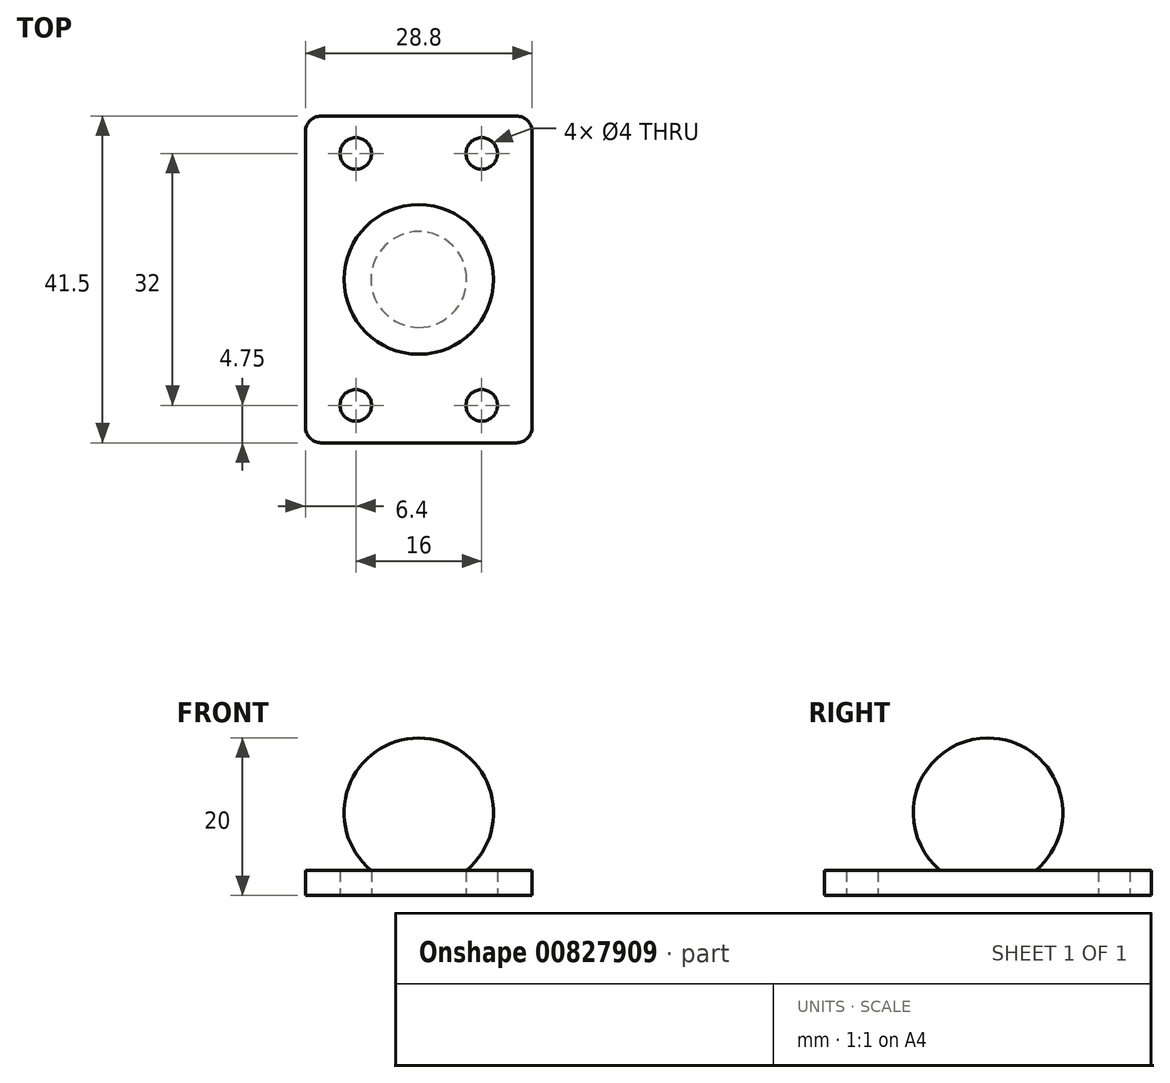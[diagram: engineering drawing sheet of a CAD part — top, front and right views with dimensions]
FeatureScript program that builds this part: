
annotation { "Feature Type Name" : "Feature", "Feature Type Description" : "" }
export const myFeature = defineFeature(function(context is Context, id is Id, definition is map)
    precondition{}
    {
        {
            var Q0;
            Q0=qCreatedBy(makeId("Top.planeOp"),FACE);
            var sketch = newSketch(context, id + "F0", { "sketchPlane" : qUnion([Q0])});
            skLineSegment(sketch, "E0.bottom", {"start": v(12.4, 20.75) * mm, "end": v(-12.4, 20.75) * mm});
            skLineSegment(sketch, "E0.top", {"start": v(12.4, -20.75) * mm, "end": v(-12.4, -20.75) * mm});
            skLineSegment(sketch, "E0.left", {"start": v(14.4, 18.75) * mm, "end": v(14.4, -18.75) * mm});
            skLineSegment(sketch, "E0.right", {"start": v(-14.4, 18.75) * mm, "end": v(-14.4, -18.75) * mm});
            skPoint(sketch, "E0.middle", {"position": v(0, 0) * mm});
            skLineSegment(sketch, "E1.bottom", {"start": v(8, 16) * mm, "end": v(-8, 16) * mm, "construction": true});
            skLineSegment(sketch, "E1.top", {"start": v(8, -16) * mm, "end": v(-8, -16) * mm, "construction": true});
            skLineSegment(sketch, "E1.left", {"start": v(8, 16) * mm, "end": v(8, -16) * mm, "construction": true});
            skLineSegment(sketch, "E1.right", {"start": v(-8, 16) * mm, "end": v(-8, -16) * mm, "construction": true});
            skCircle(sketch, "E2", {"center": v(-8, 16) * mm, "radius": 2 * mm});
            skCircle(sketch, "E3", {"center": v(8, 16) * mm, "radius": 2 * mm});
            skCircle(sketch, "E4", {"center": v(8, -16) * mm, "radius": 2 * mm});
            skCircle(sketch, "E5", {"center": v(-8, -16) * mm, "radius": 2 * mm});
            skPoint(sketch, "E6.visualSharp", {"position": v(-14.4, 20.75) * mm});
            skArc(sketch, "E6.filletArc", {"start": v(-12.4, 20.75) * mm, "mid": v(-13.81, 20.16) * mm, "end": v(-14.4, 18.75) * mm});
            skPoint(sketch, "E7.visualSharp", {"position": v(14.4, 20.75) * mm});
            skArc(sketch, "E7.filletArc", {"start": v(14.4, 18.75) * mm, "mid": v(13.81, 20.16) * mm, "end": v(12.4, 20.75) * mm});
            skPoint(sketch, "E8.visualSharp", {"position": v(14.4, -20.75) * mm});
            skArc(sketch, "E8.filletArc", {"start": v(12.4, -20.75) * mm, "mid": v(13.81, -20.16) * mm, "end": v(14.4, -18.75) * mm});
            skPoint(sketch, "E9.visualSharp", {"position": v(-14.4, -20.75) * mm});
            skArc(sketch, "E9.filletArc", {"start": v(-14.4, -18.75) * mm, "mid": v(-13.81, -20.16) * mm, "end": v(-12.4, -20.75) * mm});
            skSolve(sketch);
        }
        {
            var Q0;
            Q0 = qSketchRegion(id + "F0", true);
            extrude(context, id + "F1", {"entities" : qUnion([Q0]), "depth" : 3.2 * mm, "offsetDistance" : 25 * mm});
        }
        {
            var Q0;
            Q0=qCreatedBy(makeId("Right.planeOp"),FACE);
            var sketch = newSketch(context, id + "F2", { "sketchPlane" : qUnion([Q0])});
            skArc(sketch, "E10", {"start": v(0, 20) * mm, "mid": v(-9.5, 10.5) * mm, "end": v(0, 1) * mm});
            skPoint(sketch, "E11", {"position": v(0, 20) * mm});
            skLineSegment(sketch, "E12", {"start": v(0, 26.46) * mm, "end": v(0, 41.79) * mm, "construction": true});
            skLineSegment(sketch, "E13", {"start": v(0, 20) * mm, "end": v(0, 1) * mm});
            skSolve(sketch);
        }
        {
            var Q0;
            Q0 = qSketchRegion(id + "F2", true);
            var Q1;
            Q1=sQuery(id+"F2.wireOp",EDGE,"E12");
            revolve(context, id + "F3", {"operationType" : NewBodyOperationType.ADD, "surfaceOperationType" : NewSurfaceOperationType.NEW, "entities" : qUnion([Q0]), "axis" : qUnion([Q1]), "revolveType" : RevolveType.FULL});
        }
    });
